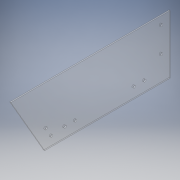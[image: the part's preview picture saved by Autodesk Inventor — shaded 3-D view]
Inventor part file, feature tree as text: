
AUTODESK INVENTOR PART (.ipt)
format: ipt  version: 2019 (Build 230136000, 136)  size: 130,560 bytes
history: native  units: in
note: dims shown in document units (in); Inventor stores cm internally (conversion verified against a paired STEP export)
features: sketch x3, hole x2, extrude x1
ambient origin geometry x8: Origin, YZ Plane, XZ Plane, XY Plane, X Axis, Y Axis, Z Axis, Center Point
bodies: Solid1 (feature_tree)
feature tree (6):
  extrude  "Extrusion1"  TaperAngle=150.0deg  [1 undecoded]
  hole  "Hole1"  [1 undecoded]
  hole  "Hole2"  [1 undecoded]
  sketch  "Sketch1"  dims[d0=3.5in d2=150.0deg]
  sketch  "Sketch2"  dims[d3=0.073in d4=0.0in d5=7.5in]
  sketch  "Sketch3"  dims[d6=0.6299in d8=0.6299in d9=0.63in d10=0.63in d11=0.63in d12=0.63in d13=6.283in d14=2.15in d15=0.15in d16=0.75in d17=0.375in d18=0.25in d19=0.5635in d20=0.432in d21=0.8108in d22=0.63in d23=0.63in d24=7.409in d25=7.09in d26=0.522in d27=0.522in d28=3.0in d29=1.5in d30=0.15in d31=0.75in d32=0.375in d33=0.25in d34=0.5635in d35=0.432in d36=0.8108in]
note: 3 required parameter values undecoded (feature->parameter linkage not recoverable at this tier; creation-order binding heuristic only, values carry confidence <= 0.55)
